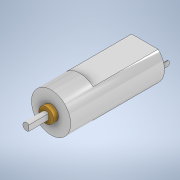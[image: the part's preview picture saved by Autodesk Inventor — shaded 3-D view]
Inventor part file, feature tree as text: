
AUTODESK INVENTOR PART (.ipt)
format: ipt  version: 2020 (Build 240168000, 168)  size: 172,032 bytes
history: native  units: in
note: dims shown in document units (in); Inventor stores cm internally (conversion verified against a paired STEP export)
features: extrude x6, sketch x6, fillet x1
ambient origin geometry x8: Origin, YZ Plane, XZ Plane, XY Plane, X Axis, Y Axis, Z Axis, Center Point
bodies: Solid1 (feature_tree)
feature tree (13):
  extrude  "Extrusion1"  Depth=0.4626in TaperAngle=0.0deg
  extrude  "Extrusion2"  Depth=1.0433in TaperAngle=0.0deg
  extrude  "Extrusion3"  Depth=0.0787in TaperAngle=0.0deg
  extrude  "Extrusion4"  Depth=0.1181in
  extrude  "Extrusion5"  Depth=0.315in
  extrude  "Extrusion7"  Depth=0.0098in
  fillet  "Fillet2"  Radius=0.0787in
  sketch  "Sketch3"  dims[d1=0.6299in d2=0.4626in d3=0.0in]
  sketch  "Sketch4"  dims[d6=0.4646in d7=1.0433in d8=0.0in]
  sketch  "Sketch5"  dims[d9=0.2362in d10=0.0787in d11=0.0in]
  sketch  "Sketch6"  dims[d12=0.1181in d13=0.0394in]
  sketch  "Sketch7"  dims[d14=0.315in d15=0.0in d16=0.2323in]
  sketch  "Sketch10"  dims[d17=0.0591in d18=0.0in d23=0.0098in d24=0.0787in d25=0.5118in d26=0.1378in d27=0.0in d28=0.0315in]
